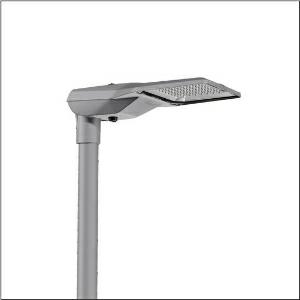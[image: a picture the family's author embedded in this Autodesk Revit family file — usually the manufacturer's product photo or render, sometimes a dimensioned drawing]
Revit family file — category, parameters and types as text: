
# Revit family: streetlight_sl_21_iq_midi___st1_0a_5xe3d51y08nb_3932
name_source: partatom
category: Lighting Fixtures
units: mm (PartAtom-declared; Revit-internal decimal feet)

## family parameters
Cut with Voids When Loaded = No
Host = Face
Light Source = No
Part Type = Normal
Room Calculation Point = No
Round Connector Dimension = Use Diameter
Shared = No

## types (1)
- --- (1 x LED, 18920 lm, 136.6 W, 3000K)
    Apparent Load = 137 VA
    CIE Flux Codes = 40 73 97 100 100
    Color Rendering = 80
    Color Temperature = 3000K
    Default Elevation = 1800 mm
    Description = Streetlight SL 21 iQ midi, mast luminaire, primary light control with lens, of PMMA, primary optical cover: cover, of toughened safety glass, transparent, light distribution: ST1.0a, light emission: direct distribution, primary light characteristic: asymmetric, installation type: post-top, side-entry, LED, High Power LED, rated luminous flux: 18.920lm, luminous efficacy: 139lm/W, light colour: 830, colour temperature: 3000K, control gear: iQ-Street Remote, D4i with power reduction, control: pre-setting: logarithmic dimming characteristic, Street-Remote, Auto-Match, Temp-Guard, Lumen-Switch, Night-Set, Smart-Wire, Light-Fading, Desk-Remote (wireless, voltage-free reading and setting of iQ features in the workshop via application-optimized NFC function/RFID function), optimised constant luminous flux control (CLO 2.0), mains connection: 230..240V, AC, 50/60Hz, start of lifetime: 137W, end of service life: 144W, reduction: 61W, luminaire housing, of diecast aluminium, powder-coated, Siteco® metallic grey (DB 702S), corrosivity category C5 mid according to DIN EN ISO 12944, please order mast flange separately, inclination adjustable: 0°, 5°, 10°, 15°, sealing non-destructively replaceable, multi-level sealing system, length: 644mm, width: 335mm, height: 110mm, mast flange for spigot size: 42mm (side-entry): 5XC10008XM4, 60/48mm (side-entry/post-top): 5XC10108XM2, 76/60mm (side-entry/post-top): 5XC10108XM1, mounting height: 4..8m, Smart Interface below and above, protection rating (complete): IP66, insulation class (complete): insulation class II (safety insulation), certification: CE, ENEC, ENEC+, VDE, impact resistance: IK10, permissible operating ambient temperature for outdoor applications: -40..+50°C, standard-compliant lighting for roads and squares, packaging unit: 1 piece

Light Distribution: ST1.0a
    Height = 111 mm
    Lamp = 1 x LED
    Lamp Light Flux = 18920 lm
    Lamp Power = 136.6 W
    Lamp count = 1
    Length = 644 mm
    Luminous efficacy = 139 lm/W
    Manufacturer = Siteco
    ModVariant = No
    Model = 5XE3D51Y08NB
    Number of Poles = 1
    OnlyDefault = Yes
    Power Factor = 1
    Product Name = Streetlight SL 21 iQ midi | ST1.0a
    Product group = mast luminaire | pylon top
    ProductGroupID = 6100
    Protection Class = Protection class II
    Protection Degree = IP 66
    RLX_Detail_Level = 1
    RLX_Emergency_Light_Flux = 0 lm
    RLX_Emergency_Type = 0
    RLX_Emergency_Type_DB = No
    RlxData = <blob elided: 92097 chars, md5=a05c419d>
    Socket = socket
    Standby Power = 0 W
    System Light Flux = 18920 lm
    System Power = 137 W
    Type Comments = factory setting: luminous flux: 100 % | dim-lin: 254 | 733 mA
    Type Image = l_1004304.jpg
    URL = http://relux.com
    VarID = @adj_135245
    Voltage = 0 V
    Weight = 0.00 kg
    Width = 336 mm

## geometry (parser evidence)
native form markers: Blend x4, Sweep x11
no freeform markers — native parametric forms only
